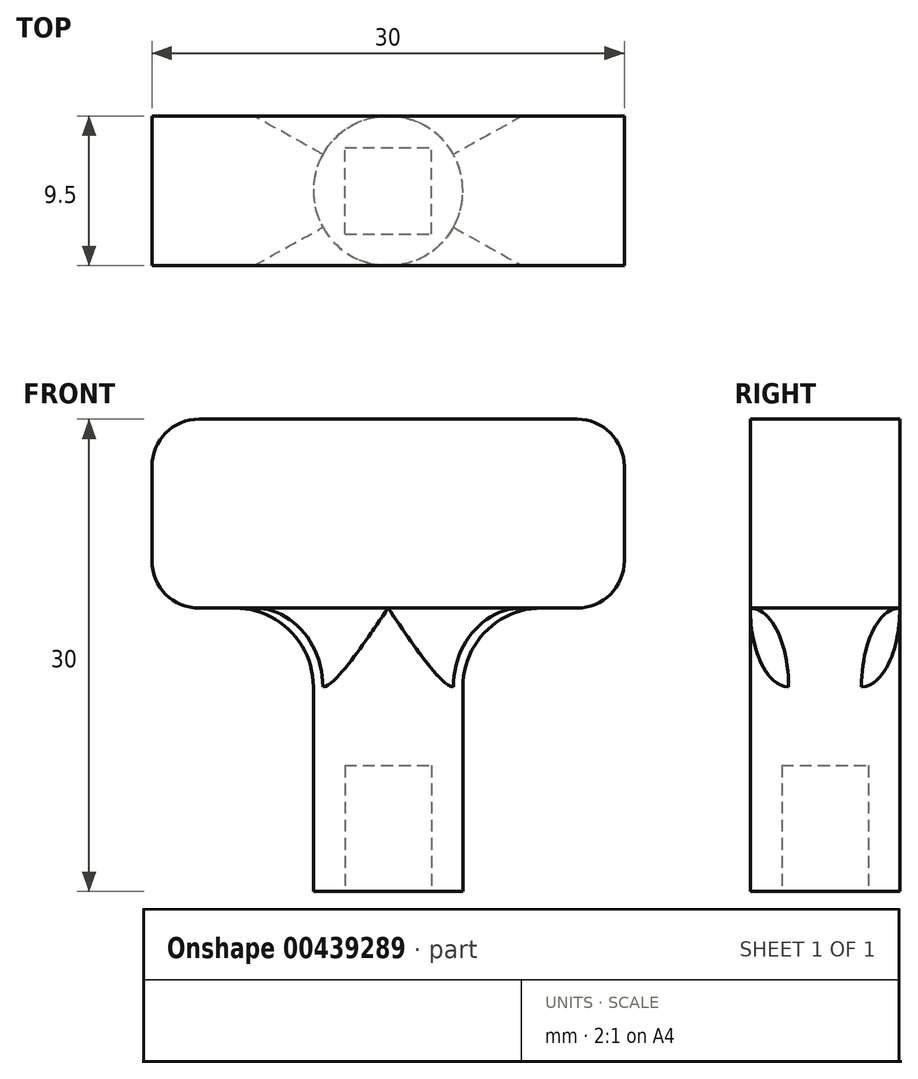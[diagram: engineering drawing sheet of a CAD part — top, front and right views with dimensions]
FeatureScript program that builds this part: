
annotation { "Feature Type Name" : "Feature", "Feature Type Description" : "" }
export const myFeature = defineFeature(function(context is Context, id is Id, definition is map)
    precondition{}
    {
        {
            var Q0;
            Q0=qCreatedBy(makeId("Top.planeOp"),FACE);
            var sketch = newSketch(context, id + "F0", { "sketchPlane" : qUnion([Q0])});
            skPoint(sketch, "E0.middle", {"position": v(0, 0) * mm});
            skCircle(sketch, "E1", {"center": v(0, 0) * mm, "radius": 4.75 * mm});
            skSolve(sketch);
        }
        {
            var Q0;
            Q0=makeQuery(id+"F0.imprint","IMPRINT",FACE,{"disambiguationData":[TD([[makeQuery(id+"F0.imprint","IMPRINT",EDGE,{"derivedFrom":sQuery(id+"F0.wireOp",EDGE,"E1")}),1.0]])]});
            extrude(context, id + "F1", {"entities" : qUnion([Q0]), "depth" : 30 * mm});
        }
        {
            var Q0;
            Q0=qCreatedBy(makeId("Front.planeOp"),FACE);
            var sketch = newSketch(context, id + "F2", { "sketchPlane" : qUnion([Q0])});
            skLineSegment(sketch, "E2.bottom", {"start": v(-12, 18) * mm, "end": v(0, 18) * mm});
            skLineSegment(sketch, "E2.top", {"start": v(-12, 30) * mm, "end": v(0, 30) * mm});
            skLineSegment(sketch, "E2.left", {"start": v(-15, 21) * mm, "end": v(-15, 27) * mm});
            skLineSegment(sketch, "E3.MirrorCS", {"start": v(12, 30) * mm, "end": v(0, 30) * mm});
            skLineSegment(sketch, "E4.MirrorCS", {"start": v(15, 21) * mm, "end": v(15, 27) * mm});
            skLineSegment(sketch, "E5.MirrorCS", {"start": v(12, 18) * mm, "end": v(0, 18) * mm});
            skPoint(sketch, "E6.visualSharp", {"position": v(-15, 30) * mm});
            skArc(sketch, "E6.filletArc", {"start": v(-12, 30) * mm, "mid": v(-14.12, 29.12) * mm, "end": v(-15, 27) * mm});
            skPoint(sketch, "E7.visualSharp", {"position": v(-15, 18) * mm});
            skArc(sketch, "E7.filletArc", {"start": v(-15, 21) * mm, "mid": v(-14.12, 18.88) * mm, "end": v(-12, 18) * mm});
            skArc(sketch, "E8.MirrorCS", {"start": v(12, 30) * mm, "mid": v(14.12, 29.12) * mm, "end": v(15, 27) * mm});
            skArc(sketch, "E9.MirrorCS", {"start": v(15, 21) * mm, "mid": v(14.12, 18.88) * mm, "end": v(12, 18) * mm});
            skPoint(sketch, "E10.orphan", {"position": v(15, 30) * mm});
            skPoint(sketch, "E11.orphan", {"position": v(15, 18) * mm});
            skSolve(sketch);
        }
        {
            var Q0;
            Q0=makeQuery(id+"F2.imprint","IMPRINT",FACE,{"disambiguationData":[TD([[makeQuery(id+"F2.imprint","IMPRINT",EDGE,{"derivedFrom":sQuery(id+"F2.wireOp",EDGE,"E2.bottom")}),1.0]])]});
            extrude(context, id + "F3", {"entities" : qUnion([Q0]), "operationType" : NewBodyOperationType.ADD, "endBound" : BoundingType.SYMMETRIC, "oppositeDirection" : true, "depth" : 9.5 * mm});
        }
        {
            var Q0;
            Q0=makeQuery(id+"F1.opExtrude","CAP_FACE",FACE,{"disambiguationData":[OSD([sQuery(id+"F0.wireOp",EDGE,"E1")])],"isStart":true});
            var sketch = newSketch(context, id + "F4", { "sketchPlane" : qUnion([Q0])});
            skLineSegment(sketch, "E12.bottom", {"start": v(-2.75, 2.75) * mm, "end": v(2.75, 2.75) * mm});
            skLineSegment(sketch, "E12.top", {"start": v(-2.75, -2.75) * mm, "end": v(2.75, -2.75) * mm});
            skLineSegment(sketch, "E12.left", {"start": v(-2.75, 2.75) * mm, "end": v(-2.75, -2.75) * mm});
            skLineSegment(sketch, "E12.right", {"start": v(2.75, 2.75) * mm, "end": v(2.75, -2.75) * mm});
            skPoint(sketch, "E12.middle", {"position": v(0, 0) * mm});
            skSolve(sketch);
        }
        {
            var Q0;
            Q0=makeQuery(id+"F4.imprint","IMPRINT",FACE,{"disambiguationData":[TD([[makeQuery(id+"F4.imprint","IMPRINT",EDGE,{"derivedFrom":sQuery(id+"F4.wireOp",EDGE,"E12.bottom")}),-1.0]])]});
            extrude(context, id + "F5", {"entities" : qUnion([Q0]), "operationType" : NewBodyOperationType.REMOVE, "oppositeDirection" : true, "depth" : 8 * mm});
        }
        {
            var Q0;
            Q0=makeQuery(id+"F3.boolean.opBoolean","INTERSECT",EDGE,{"disambiguationData":[OD(0.0)],"derivedFrom":[makeQuery(id+"F1.opExtrude","SWEPT_FACE",FACE,{"disambiguationData":[OSD([sQuery(id+"F0.wireOp",EDGE,"E1")])]}),makeQuery(id+"F3.opExtrude","SWEPT_FACE",FACE,{"disambiguationData":[OSD([sQuery(id+"F2.wireOp",EDGE,"E2.bottom"),sQuery(id+"F2.wireOp",EDGE,"E5.MirrorCS")])]})]});
            fillet(context, id + "F6", {"entities" : qUnion([Q0]), "radius" : 5 * mm, "tangentPropagation" : true, "allowEdgeOverflow" : false});
        }
    });
